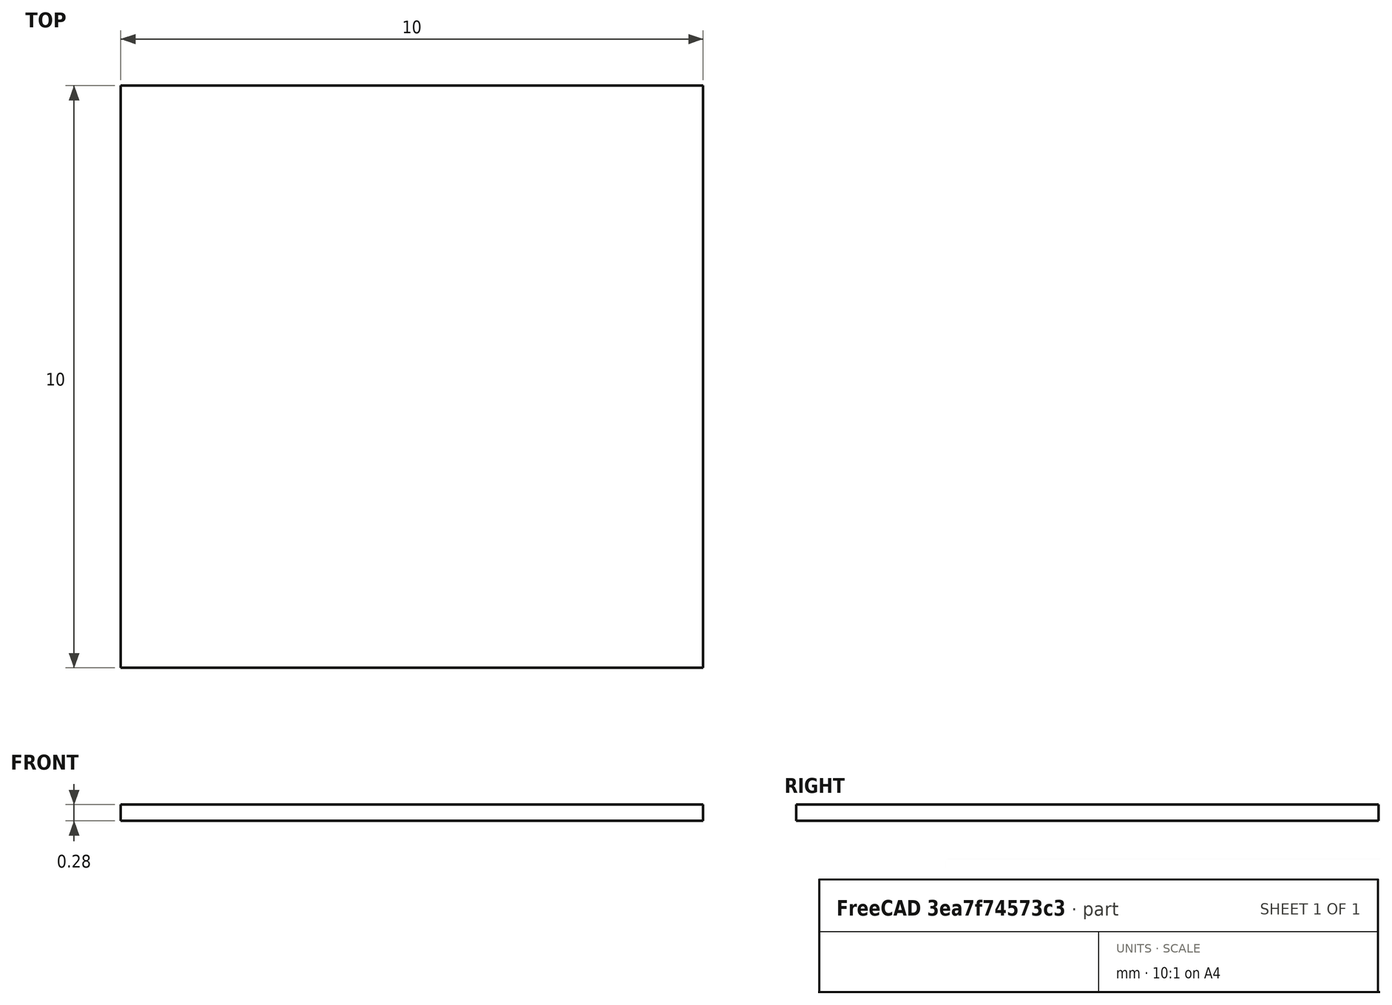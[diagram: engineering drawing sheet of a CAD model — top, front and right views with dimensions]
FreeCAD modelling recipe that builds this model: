
FCSTD DOCUMENT  (FreeCAD 0.18.4R)
Label: Sample_Holder_FP_Dummy
License: All rights reserved
LicenseURL: http://en.wikipedia.org/wiki/All_rights_reserved
objects: Sketcher::SketchObject×1, PartDesign::Pad×1, PartDesign::Body×1
note: 4 computed .brp shape members not serialized (recipe doc carries the construction recipe); baked Part::Feature solids carry a one-line shape summary decoded from their .brp

FEATURE [Sketcher::SketchObject] Sketch
  MapMode = 5
  Support = -> [XY_Plane]
  sketch-geometry (4):
    g0: LineSegment StartX=-5 StartY=5 StartZ=0 EndX=5 EndY=5 EndZ=0
    g1: LineSegment StartX=5 StartY=5 StartZ=0 EndX=5 EndY=-5 EndZ=0
    g2: LineSegment StartX=5 StartY=-5 StartZ=0 EndX=-5 EndY=-5 EndZ=0
    g3: LineSegment StartX=-5 StartY=-5 StartZ=0 EndX=-5 EndY=5 EndZ=0
  constraints (12):
    c: Coincident(g0,g1)
    c: Coincident(g1,g2)
    c: Coincident(g2,g3)
    c: Coincident(g3,g0)
    c: Horizontal(g0)
    c: Horizontal(g2)
    c: Vertical(g1)
    c: Vertical(g3)
    c: DistanceY(g1,g1) = 10
    c: DistanceX(g0,g0) = 10
    c: DistanceX(g-1,g1) = 5
    c: DistanceY(g2,g-1) = 5
FEATURE [PartDesign::Pad] Pad
  Length = 0.28
  Length2 = 100
  Profile = -> Sketch
  Type = 0
FEATURE [PartDesign::Body] Body
  Group = -> [Sketch,Pad]
  Origin = -> Origin
  Tip = -> Pad
